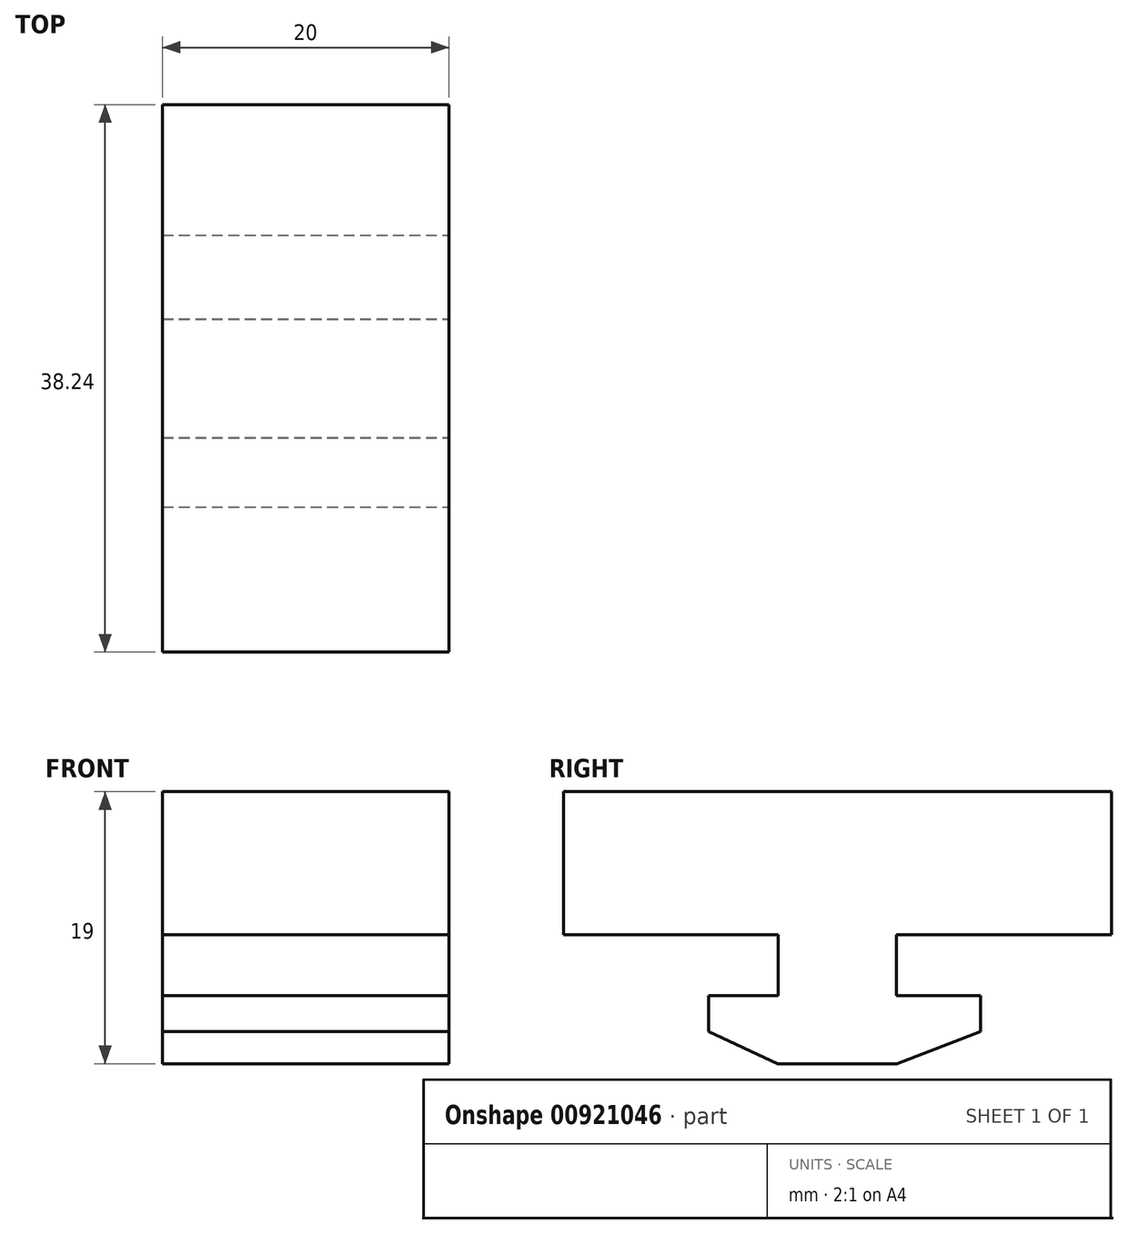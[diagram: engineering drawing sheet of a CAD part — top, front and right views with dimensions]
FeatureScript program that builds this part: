
annotation { "Feature Type Name" : "Feature", "Feature Type Description" : "" }
export const myFeature = defineFeature(function(context is Context, id is Id, definition is map)
    precondition{}
    {
        {
            var Q0;
            Q0=qCreatedBy(makeId("Top.planeOp"),FACE);
            var sketch = newSketch(context, id + "F0", { "sketchPlane" : qUnion([Q0])});
            skLineSegment(sketch, "E0.bottom", {"start": v(10, -19.12) * mm, "end": v(-10, -19.12) * mm});
            skLineSegment(sketch, "E0.top", {"start": v(10, 19.13) * mm, "end": v(-10, 19.13) * mm});
            skLineSegment(sketch, "E0.left", {"start": v(10, -19.12) * mm, "end": v(10, 19.13) * mm});
            skLineSegment(sketch, "E0.right", {"start": v(-10, -19.12) * mm, "end": v(-10, 19.12) * mm});
            skPoint(sketch, "E0.middle", {"position": v(0, 0) * mm});
            skSolve(sketch);
        }
        {
            var Q0;
            Q0=makeQuery(id+"F0.imprint","IMPRINT",FACE,{"disambiguationData":[TD([[makeQuery(id+"F0.imprint","IMPRINT",EDGE,{"derivedFrom":sQuery(id+"F0.wireOp",EDGE,"E0.bottom")}),-1.0]])]});
            extrude(context, id + "F1", {"entities" : qUnion([Q0]), "depth" : 10 * mm, "offsetDistance" : 25 * mm});
        }
        {
            var Q0;
            Q0=makeQuery(id+"F1.opExtrude","SWEPT_FACE",FACE,{"disambiguationData":[OSD([sQuery(id+"F0.wireOp",EDGE,"E0.left")])]});
            var sketch = newSketch(context, id + "F2", { "sketchPlane" : qUnion([Q0])});
            skLineSegment(sketch, "E1", {"start": v(0, 0) * mm, "end": v(0, -9) * mm});
            skLineSegment(sketch, "E2", {"start": v(0, -4.25) * mm, "end": v(-9, -4.25) * mm});
            skLineSegment(sketch, "E3", {"start": v(0, -4.25) * mm, "end": v(10, -4.25) * mm});
            skLineSegment(sketch, "E4", {"start": v(-9, -4.25) * mm, "end": v(-9, -6.75) * mm});
            skLineSegment(sketch, "E5", {"start": v(10, -4.25) * mm, "end": v(10, -6.75) * mm});
            skLineSegment(sketch, "E6", {"start": v(0, -9) * mm, "end": v(4.15, -9) * mm});
            skLineSegment(sketch, "E7", {"start": v(0, -9) * mm, "end": v(-4.15, -9) * mm});
            skLineSegment(sketch, "E8", {"start": v(-4.15, -9) * mm, "end": v(-9, -6.75) * mm});
            skLineSegment(sketch, "E9", {"start": v(4.15, -9) * mm, "end": v(10, -6.75) * mm});
            skLineSegment(sketch, "E10", {"start": v(0, 0) * mm, "end": v(4.12, 0) * mm});
            skLineSegment(sketch, "E11", {"start": v(0, 0) * mm, "end": v(-4.13, 0) * mm});
            skLineSegment(sketch, "E12", {"start": v(-4.13, 0) * mm, "end": v(-4.13, -4.25) * mm});
            skLineSegment(sketch, "E13", {"start": v(4.12, 0) * mm, "end": v(4.12, -4.25) * mm});
            skSolve(sketch);
        }
        {
            var Q0;
            Q0 = qSketchRegion(id + "F2", true);
            extrude(context, id + "F3", {"entities" : qUnion([Q0]), "operationType" : NewBodyOperationType.ADD, "oppositeDirection" : true, "depth" : 20 * mm, "offsetDistance" : 25 * mm});
        }
    });
